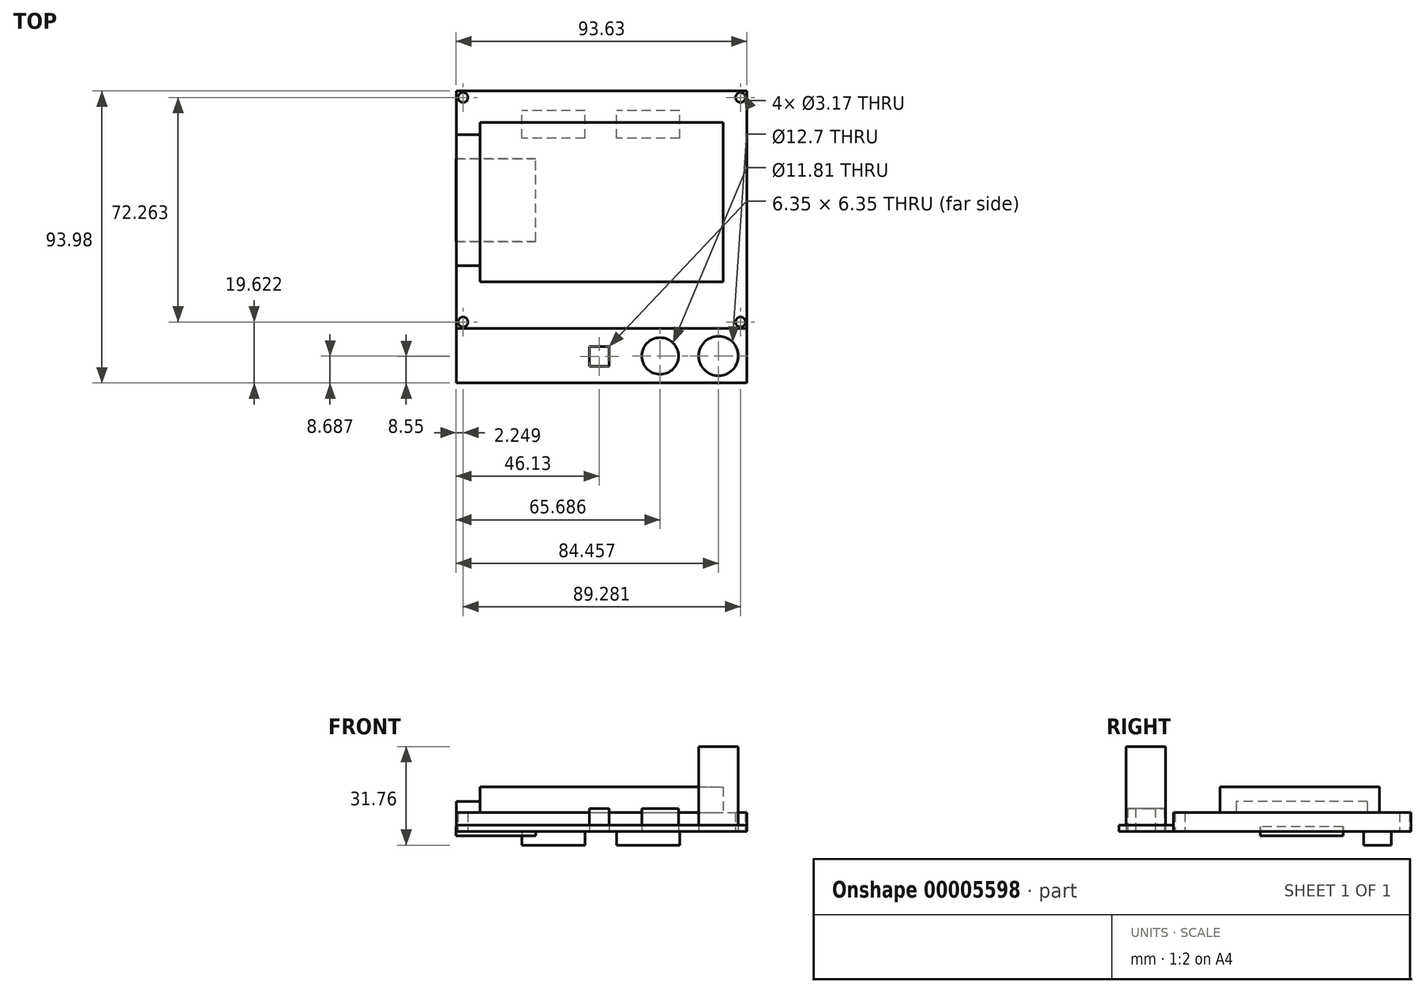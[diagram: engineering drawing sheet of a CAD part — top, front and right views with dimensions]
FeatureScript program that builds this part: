
annotation { "Feature Type Name" : "Feature", "Feature Type Description" : "" }
export const myFeature = defineFeature(function(context is Context, id is Id, definition is map)
    precondition{}
    {
        {
            var Q0;
            Q0=qCreatedBy(makeId("Top.planeOp"),FACE);
            var sketch = newSketch(context, id + "F0", { "sketchPlane" : qUnion([Q0])});
            skLineSegment(sketch, "E0.bottom", {"start": v(-46.74, 47) * mm, "end": v(46.74, 47) * mm, "construction": true});
            skLineSegment(sketch, "E0.top", {"start": v(-46.74, -47) * mm, "end": v(46.74, -47) * mm, "construction": true});
            skLineSegment(sketch, "E0.left", {"start": v(-46.74, 47) * mm, "end": v(-46.74, -47) * mm, "construction": true});
            skLineSegment(sketch, "E0.right", {"start": v(46.74, 47) * mm, "end": v(46.74, -47) * mm, "construction": true});
            skLineSegment(sketch, "E1.bottom", {"start": v(-39.12, 36.83) * mm, "end": v(39.12, 36.83) * mm});
            skLineSegment(sketch, "E1.top", {"start": v(-39.12, -14.48) * mm, "end": v(39.12, -14.48) * mm});
            skLineSegment(sketch, "E1.left", {"start": v(-39.12, 36.83) * mm, "end": v(-39.12, -14.48) * mm});
            skLineSegment(sketch, "E1.right", {"start": v(39.12, 36.83) * mm, "end": v(39.12, -14.48) * mm});
            skLineSegment(sketch, "E2.bottom", {"start": v(-46.74, 47) * mm, "end": v(46.74, 47) * mm});
            skLineSegment(sketch, "E2.top", {"start": v(-46.74, -29.46) * mm, "end": v(46.74, -29.46) * mm});
            skLineSegment(sketch, "E2.left", {"start": v(-46.74, 47) * mm, "end": v(-46.74, -29.46) * mm});
            skLineSegment(sketch, "E2.right", {"start": v(46.74, 47) * mm, "end": v(46.74, -29.46) * mm});
            skLineSegment(sketch, "E3.top", {"start": v(-46.74, -47) * mm, "end": v(46.74, -47) * mm});
            skLineSegment(sketch, "E3.left", {"start": v(-46.74, -29.46) * mm, "end": v(-46.74, -47) * mm});
            skLineSegment(sketch, "E3.right", {"start": v(46.74, -29.46) * mm, "end": v(46.74, -47) * mm});
            skLineSegment(sketch, "E4.bottom", {"start": v(-46.74, 32.94) * mm, "end": v(-39.12, 32.94) * mm});
            skLineSegment(sketch, "E4.top", {"start": v(-46.74, -9.22) * mm, "end": v(-39.12, -9.22) * mm});
            skLineSegment(sketch, "E4.left", {"start": v(-46.74, 32.94) * mm, "end": v(-46.74, -9.22) * mm});
            skLineSegment(sketch, "E4.right", {"start": v(-39.12, 32.94) * mm, "end": v(-39.12, -9.22) * mm});
            skCircle(sketch, "E5", {"center": v(37.57, -38.3) * mm, "radius": 6.35 * mm});
            skCircle(sketch, "E6", {"center": v(18.8, -38.3) * mm, "radius": 5.9 * mm});
            skLineSegment(sketch, "E7.bottom", {"start": v(-3.93, -35.27) * mm, "end": v(2.42, -35.27) * mm});
            skLineSegment(sketch, "E7.top", {"start": v(-3.93, -41.62) * mm, "end": v(2.42, -41.62) * mm});
            skLineSegment(sketch, "E7.left", {"start": v(-3.93, -35.27) * mm, "end": v(-3.93, -41.62) * mm});
            skLineSegment(sketch, "E7.right", {"start": v(2.42, -35.27) * mm, "end": v(2.42, -41.62) * mm});
            skCircle(sketch, "E8", {"center": v(-44.64, -27.37) * mm, "radius": 1.59 * mm});
            skCircle(sketch, "E9", {"center": v(44.64, -27.37) * mm, "radius": 1.59 * mm});
            skCircle(sketch, "E10", {"center": v(44.64, 44.9) * mm, "radius": 1.59 * mm});
            skCircle(sketch, "E11", {"center": v(-44.64, 44.9) * mm, "radius": 1.59 * mm});
            skSolve(sketch);
        }
        {
            var Q0;
            {var subQ3=sQuery(id+"F0.wireOp",EDGE,"E1.bottom");Q0=makeQuery(id+"F0.imprint","IMPRINT",FACE,{"disambiguationData":[TD([[makeQuery(id+"F0.imprint","IMPRINT",EDGE,{"derivedFrom":subQ3}),-1.0]])]});}
            extrude(context, id + "F1", {"entities" : qUnion([Q0]), "depth" : 14.25 * mm});
        }
        {
            var Q0;
            Q0=makeQuery(id+"F0.imprint","IMPRINT",FACE,{"disambiguationData":[TD([[makeQuery(id+"F0.imprint","IMPRINT",EDGE,{"derivedFrom":sQuery(id+"F0.wireOp",EDGE,"E4.bottom")}),-1.0]])]});
            extrude(context, id + "F2", {"entities" : qUnion([Q0]), "operationType" : NewBodyOperationType.ADD, "depth" : 9.6 * mm});
        }
        {
            var Q0;
            {var subQ9=sQuery(id+"F0.wireOp",EDGE,"E1.bottom");Q0=makeQuery(id+"F0.imprint","IMPRINT",FACE,{"disambiguationData":[TD([[makeQuery(id+"F0.imprint","IMPRINT",EDGE,{"derivedFrom":subQ9}),1.0]])]});}
            extrude(context, id + "F3", {"entities" : qUnion([Q0]), "operationType" : NewBodyOperationType.ADD, "depth" : 6 * mm});
        }
        {
            var Q0;
            Q0=makeQuery(id+"F0.imprint","IMPRINT",FACE,{"disambiguationData":[TD([[makeQuery(id+"F0.imprint","IMPRINT",EDGE,{"derivedFrom":sQuery(id+"F0.wireOp",EDGE,"E5")}),1.0]])]});
            extrude(context, id + "F4", {"entities" : qUnion([Q0]), "depth" : 27.3 * mm});
        }
        {
            var Q0;
            Q0=makeQuery(id+"F0.imprint","IMPRINT",FACE,{"disambiguationData":[TD([[makeQuery(id+"F0.imprint","IMPRINT",EDGE,{"derivedFrom":sQuery(id+"F0.wireOp",EDGE,"E6")}),1.0]])]});
            extrude(context, id + "F5", {"entities" : qUnion([Q0]), "depth" : 7.37 * mm});
        }
        {
            var Q0;
            Q0=makeQuery(id+"F0.imprint","IMPRINT",FACE,{"disambiguationData":[TD([[makeQuery(id+"F0.imprint","IMPRINT",EDGE,{"derivedFrom":sQuery(id+"F0.wireOp",EDGE,"E7.bottom")}),-1.0]])]});
            extrude(context, id + "F6", {"entities" : qUnion([Q0]), "depth" : 7.37 * mm});
        }
        {
            var Q0;
            Q0=makeQuery(id+"F0.imprint","IMPRINT",FACE,{"disambiguationData":[TD([[makeQuery(id+"F0.imprint","IMPRINT",EDGE,{"derivedFrom":sQuery(id+"F0.wireOp",EDGE,"E2.top")}),-1.0]])]});
            extrude(context, id + "F7", {"entities" : qUnion([Q0]), "depth" : 2 * mm});
        }
        {
            var Q0;
            Q0=qCreatedBy(makeId("Top.planeOp"),FACE);
            var sketch = newSketch(context, id + "F8", { "sketchPlane" : qUnion([Q0])});
            skLineSegment(sketch, "E12.bottom", {"start": v(-46.9, -47.04) * mm, "end": v(46.79, -47.04) * mm});
            skLineSegment(sketch, "E12.top", {"start": v(-46.9, 47.08) * mm, "end": v(46.79, 47.08) * mm});
            skLineSegment(sketch, "E12.left", {"start": v(-46.9, -47.04) * mm, "end": v(-46.9, 47.08) * mm});
            skLineSegment(sketch, "E12.right", {"start": v(46.79, -47.04) * mm, "end": v(46.79, 47.08) * mm});
            skLineSegment(sketch, "E13.bottom", {"start": v(-25.76, 40.73) * mm, "end": v(-5.44, 40.73) * mm});
            skLineSegment(sketch, "E13.top", {"start": v(-25.76, 31.74) * mm, "end": v(-5.44, 31.74) * mm});
            skLineSegment(sketch, "E13.left", {"start": v(-25.76, 40.73) * mm, "end": v(-25.76, 31.74) * mm});
            skLineSegment(sketch, "E13.right", {"start": v(-5.44, 40.73) * mm, "end": v(-5.44, 31.74) * mm});
            skLineSegment(sketch, "E14.bottom", {"start": v(4.72, 40.73) * mm, "end": v(25.04, 40.73) * mm});
            skLineSegment(sketch, "E14.top", {"start": v(4.72, 31.74) * mm, "end": v(25.04, 31.74) * mm});
            skLineSegment(sketch, "E14.left", {"start": v(4.72, 40.73) * mm, "end": v(4.72, 31.74) * mm});
            skLineSegment(sketch, "E14.right", {"start": v(25.04, 40.73) * mm, "end": v(25.04, 31.74) * mm});
            skLineSegment(sketch, "E15.bottom", {"start": v(-46.9, 25.18) * mm, "end": v(-21.24, 25.18) * mm});
            skLineSegment(sketch, "E15.top", {"start": v(-46.9, -1.49) * mm, "end": v(-21.24, -1.49) * mm});
            skLineSegment(sketch, "E15.left", {"start": v(-46.9, 25.18) * mm, "end": v(-46.9, -1.49) * mm});
            skLineSegment(sketch, "E15.right", {"start": v(-21.24, 25.18) * mm, "end": v(-21.24, -1.49) * mm});
            skSolve(sketch);
        }
        {
            var Q0;
            Q0=makeQuery(id+"F8.imprint","IMPRINT",FACE,{"disambiguationData":[TD([[makeQuery(id+"F8.imprint","IMPRINT",EDGE,{"derivedFrom":sQuery(id+"F8.wireOp",EDGE,"E15.bottom")}),-1.0]])]});
            extrude(context, id + "F9", {"entities" : qUnion([Q0]), "operationType" : NewBodyOperationType.ADD, "depth" : 2.9 * mm, "symmetric" : true});
        }
        {
            var Q0;
            Q0=makeQuery(id+"F8.imprint","IMPRINT",FACE,{"disambiguationData":[TD([[makeQuery(id+"F8.imprint","IMPRINT",EDGE,{"derivedFrom":sQuery(id+"F8.wireOp",EDGE,"E14.bottom")}),-1.0]])]});
            var Q1;
            Q1=makeQuery(id+"F8.imprint","IMPRINT",FACE,{"disambiguationData":[TD([[makeQuery(id+"F8.imprint","IMPRINT",EDGE,{"derivedFrom":sQuery(id+"F8.wireOp",EDGE,"E13.bottom")}),-1.0]])]});
            extrude(context, id + "F10", {"entities" : qUnion([Q0, Q1]), "operationType" : NewBodyOperationType.ADD, "depth" : 8.9 * mm, "symmetric" : true});
        }
    });
